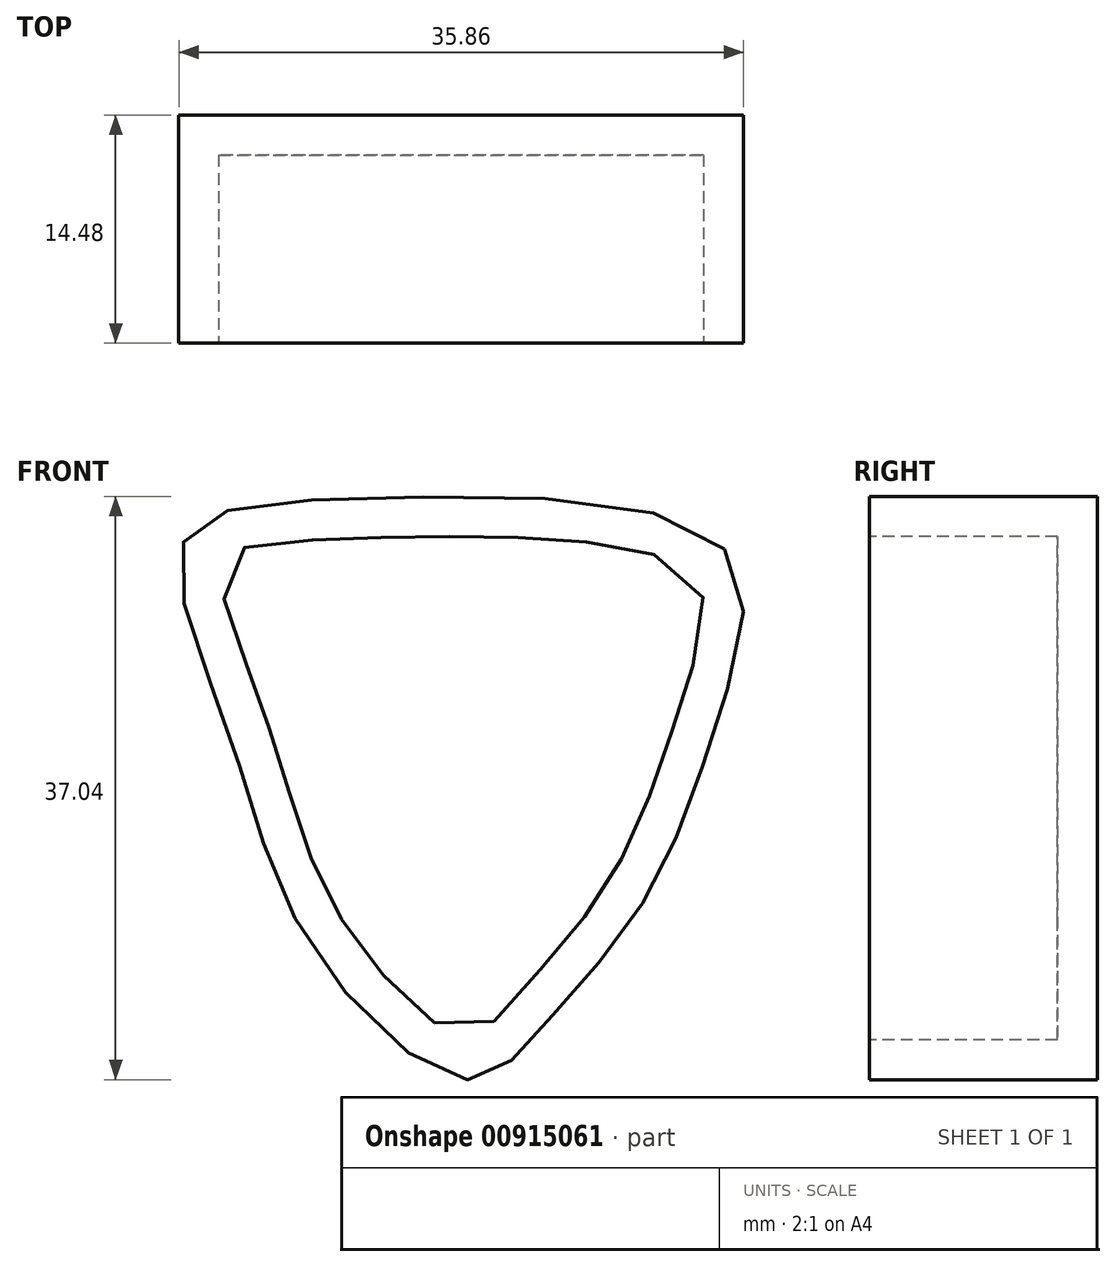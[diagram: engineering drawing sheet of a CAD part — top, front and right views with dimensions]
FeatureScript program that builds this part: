
annotation { "Feature Type Name" : "Feature", "Feature Type Description" : "" }
export const myFeature = defineFeature(function(context is Context, id is Id, definition is map)
    precondition{}
    {
        {
            var Q0;
            Q0=qCreatedBy(makeId("Top.planeOp"),FACE);
            var sketch = newSketch(context, id + "F0", { "sketchPlane" : qUnion([Q0])});
            skLineSegment(sketch, "E0.bottom", {"start": v(-35.33, 23.37) * mm, "end": v(35.33, 23.37) * mm});
            skLineSegment(sketch, "E0.top", {"start": v(-35.33, -23.37) * mm, "end": v(35.33, -23.37) * mm});
            skLineSegment(sketch, "E0.left", {"start": v(-35.33, 23.37) * mm, "end": v(-35.33, -23.37) * mm});
            skLineSegment(sketch, "E0.right", {"start": v(35.33, 23.37) * mm, "end": v(35.33, -23.37) * mm});
            skPoint(sketch, "E0.middle", {"position": v(0, 0) * mm});
            skSolve(sketch);
        }
        {
            var Q0;
            Q0=makeQuery(id+"F0.imprint","IMPRINT",FACE,{"disambiguationData":[TD([[makeQuery(id+"F0.imprint","IMPRINT",EDGE,{"derivedFrom":sQuery(id+"F0.wireOp",EDGE,"E0.bottom")}),-1.0]])]});
            extrude(context, id + "F1", {"entities" : qUnion([Q0]), "depth" : 86.61 * mm, "offsetDistance" : 25.4 * mm});
        }
        {
            var Q0;
            Q0=makeQuery(id+"F1.opExtrude","SWEPT_FACE",FACE,{"disambiguationData":[OSD([sQuery(id+"F0.wireOp",EDGE,"E0.bottom")])]});
            var sketch = newSketch(context, id + "F2", { "sketchPlane" : qUnion([Q0])});
            skPoint(sketch, "E1.4.internal.snap0", {"position": v(1.28, 33.67) * mm});
            skFitSpline(sketch, "E1", {"points": [v(-15.21, 69.66) * mm, v(-14.75, 58.75) * mm, v(-10.1, 47.36) * mm, v(-3.37, 39) * mm, v(1.28, 35.98) * mm, v(11.27, 44.8) * mm, v(16.38, 58.28) * mm, v(19.16, 70.13) * mm, v(7.55, 72.92) * mm, v(-15.21, 69.66) * mm]});
            skLineSegment(sketch, "E2", {"start": v(-12.9, 69.66) * mm, "end": v(-12.9, 65.02) * mm});
            skLineSegment(sketch, "E3", {"start": v(-12.9, 65.02) * mm, "end": v(-11.03, 65.02) * mm});
            skLineSegment(sketch, "E4", {"start": v(-11.03, 65.02) * mm, "end": v(-11.03, 69.9) * mm});
            skLineSegment(sketch, "E5", {"start": v(-11.03, 69.9) * mm, "end": v(-9.17, 67.34) * mm});
            skLineSegment(sketch, "E6", {"start": v(-9.17, 67.34) * mm, "end": v(-9.17, 69.66) * mm});
            skLineSegment(sketch, "E7", {"start": v(-9.17, 69.66) * mm, "end": v(-9.17, 67.34) * mm});
            skSolve(sketch);
        }
        {
            var Q0;
            Q0=makeQuery(id+"F2.imprint","IMPRINT",FACE,{"disambiguationData":[TD([[makeQuery(id+"F2.imprint","IMPRINT",EDGE,{"derivedFrom":sQuery(id+"F2.wireOp",EDGE,"E1")}),-1.0]])]});
            extrude(context, id + "F3", {"entities" : qUnion([Q0]), "operationType" : NewBodyOperationType.REMOVE, "oppositeDirection" : true, "depth" : 59.44 * mm, "offsetDistance" : 25.4 * mm});
        }
        {
            var Q0;
            Q0=makeQuery(id+"F1.opExtrude","SWEPT_FACE",FACE,{"disambiguationData":[OSD([sQuery(id+"F0.wireOp",EDGE,"E0.top")])]});
            extrude(context, id + "F4", {"entities" : qUnion([Q0]), "operationType" : NewBodyOperationType.REMOVE, "oppositeDirection" : true, "depth" : 32.26 * mm, "offsetDistance" : 25.4 * mm});
        }
        {
            var Q0;
            Q0=makeQuery(id+"F4.boolean.opBoolean","COPY",FACE,{"derivedFrom":makeQuery(id+"F4.opExtrude","CAP_FACE",FACE,{"disambiguationData":[OSD([sQuery(id+"F0.wireOp",EDGE,"E0.top")])],"isStart":false})});
            shell(context, id + "F5", {"entities" : qUnion([Q0]), "thickness" : 2.54 * mm});
        }
    });
